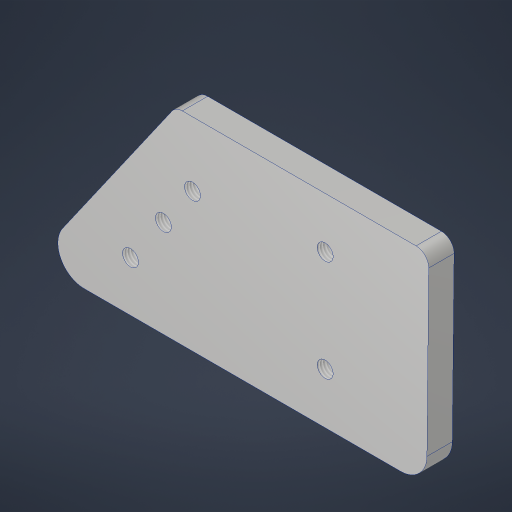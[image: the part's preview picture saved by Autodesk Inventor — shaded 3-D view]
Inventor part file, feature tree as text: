
AUTODESK INVENTOR PART (.ipt)
format: ipt  version: 2023.4 (Build 274418000, 418)  size: 257,536 bytes
history: native  units: in
note: dims shown in document units (in); Inventor stores cm internally (conversion verified against a paired STEP export)
features: sketch x5, extrude x3, hole x3, fillet x2, projected_geometry x1
ambient origin geometry x8: Origin, YZ Plane, XZ Plane, XY Plane, X Axis, Y Axis, Z Axis, Center Point
bodies: Solid1 (feature_tree)
feature tree (14):
  sketch  "Sketch1"  dims[d0=2.0in d1=15.25in]
  sketch  "Sketch2"  dims[d2=1.0in d3=17.0in d5=0.3779in]
  extrude  "Extrusion1"  Depth=2.0in
  hole  "Hole1"  [1 undecoded]
  fillet  "Fillet1"  Radius=0.3779in
  sketch  "Sketch3"  dims[d6=0.88in d7=1.875in]
  extrude  "Extrusion2"  Depth=1.875in
  hole  "Hole2"  [1 undecoded]
  extrude  "Extrusion3"  Depth=0.25in
  fillet  "Fillet2"  Radius=1.0in
  hole  "Hole3"  [1 undecoded]
  projected_geometry  "Projected Loop1"
  sketch  "Sketch4"  dims[d8=0.625in d10=0.5in]
  sketch  "Sketch5"  dims[d11=17.0in d12=4.0in d13=1.0in d14=0.5in d15=0.5in d16=0.5655in d18=0.25in d19=0.0in d20=0.156in d21=0.38in d22=0.385in d23=0.25in d24=0.5635in d25=1.0in d26=0.8108in d27=0.26in d28=1.875in d29=2.5in d30=1.5748in d32=360.0deg d34=0.125in d35=0.0in d36=0.156in d37=0.38in d38=0.385in d39=0.25in d40=0.5635in d41=1.0in d42=0.8108in d43=2.0in d44=0.0in d45=0.0in d46=0.125in d47=1.0in d48=0.5in d49=0.156in d50=0.38in d51=0.385in d52=0.25in d53=0.5635in d54=1.0in d55=0.8108in d56=1.25in]
note: 3 required parameter values undecoded (feature->parameter linkage not recoverable at this tier; creation-order binding heuristic only, values carry confidence <= 0.55)
